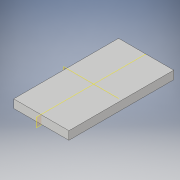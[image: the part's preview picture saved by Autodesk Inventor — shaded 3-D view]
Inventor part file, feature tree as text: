
AUTODESK INVENTOR PART (.ipt)
format: ipt  version: 2017 (Build 210142000, 142)  size: 171,520 bytes
history: native  units: in
note: dims shown in document units (in); Inventor stores cm internally (conversion verified against a paired STEP export)
features: extrude x4, sketch x4, plane x2, mirror x2, projected_geometry x1
ambient origin geometry x8: Origin, YZ Plane, XZ Plane, XY Plane, X Axis, Y Axis, Z Axis, Center Point
bodies: Solid1 (feature_tree)
feature tree (13):
  extrude  "Extrusion1"  Depth=76.0in
  extrude  "Extrusion2"  Depth=1.0in
  extrude  "Extrusion3"  Depth=2.0in TaperAngle=0.0deg
  plane  "Work Plane1"
  mirror  "Mirror1"
  extrude  "Extrusion4"  Depth=18.0in
  plane  "Work Plane2"
  mirror  "Mirror2"
  sketch  "Sketch1"  dims[d0=40.0in d1=76.0in]
  sketch  "Sketch2"  dims[d2=6.0in d3=0.0in d4=1.0in]
  sketch  "Sketch3"  dims[d5=1.0in d6=2.0in d7=0.0in]
  projected_geometry  "Projected Loop1"
  sketch  "Sketch4"  dims[d8=1.0in d9=18.0in d10=10.0in d11=1.0in d12=18.0in d13=10.0in d14=2.0in d15=0.0in d16=6.0in d17=1.0in d18=6.0in d19=1.0in d20=7.0in d21=7.0in d22=2.0in d23=0.0in]
